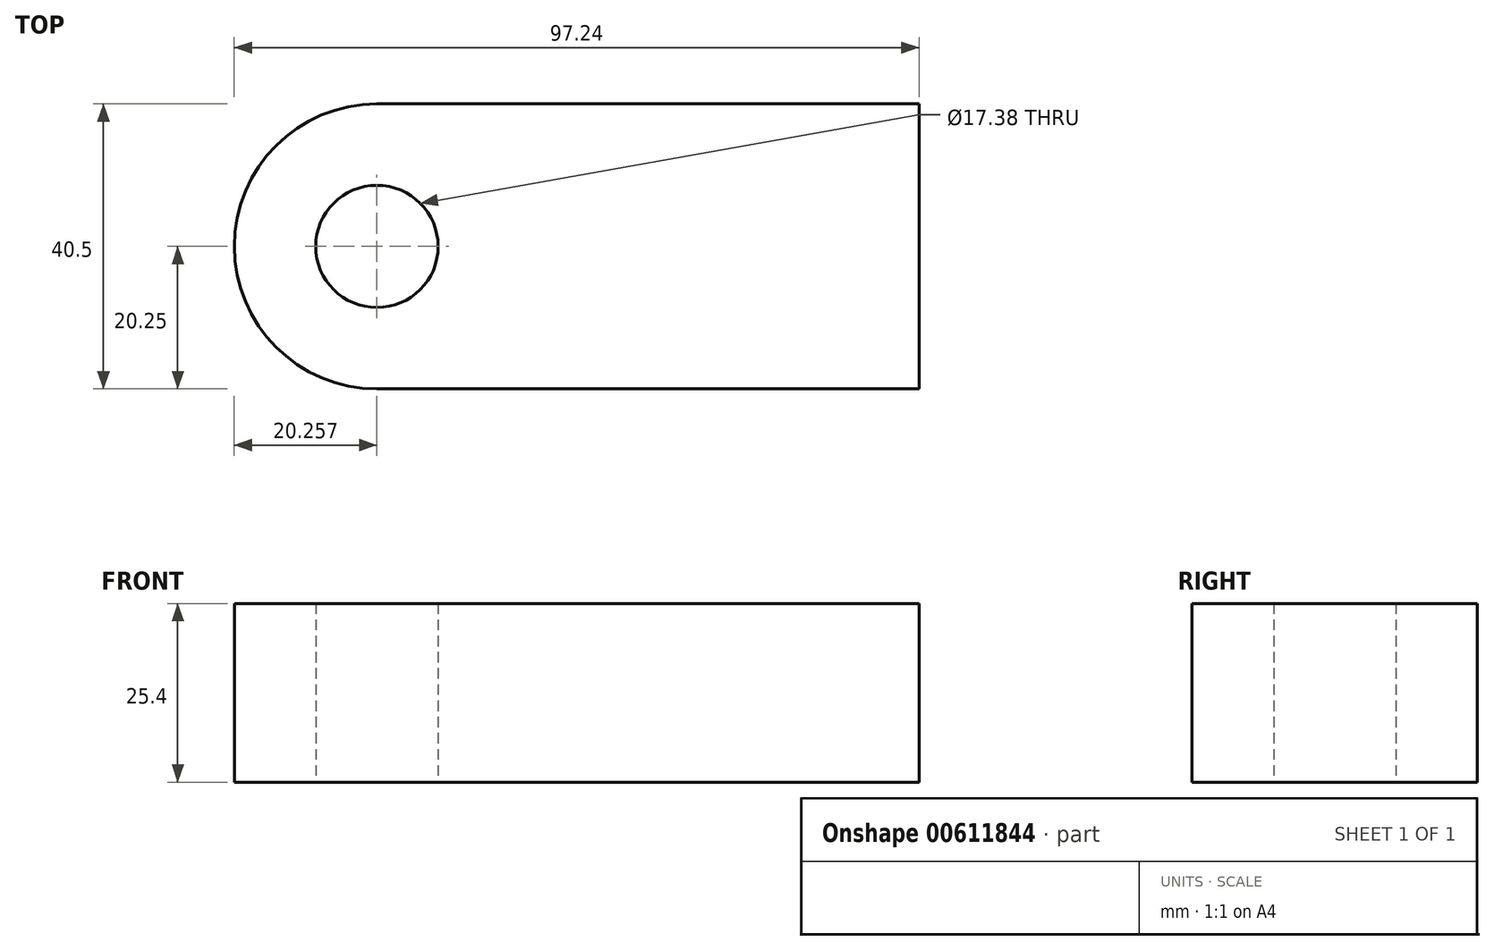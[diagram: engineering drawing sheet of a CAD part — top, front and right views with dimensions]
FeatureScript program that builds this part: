
annotation { "Feature Type Name" : "Feature", "Feature Type Description" : "" }
export const myFeature = defineFeature(function(context is Context, id is Id, definition is map)
    precondition{}
    {
        {
            var Q0;
            Q0=qCreatedBy(makeId("Top.planeOp"),FACE);
            var sketch = newSketch(context, id + "F0", { "sketchPlane" : qUnion([Q0])});
            skPoint(sketch, "E0.center.orphan", {"position": v(-43.75, 0) * mm});
            skLineSegment(sketch, "E1.bottom", {"start": v(-38.5, -20.25) * mm, "end": v(38.5, -20.25) * mm});
            skLineSegment(sketch, "E1.top", {"start": v(-38.5, 20.25) * mm, "end": v(38.5, 20.25) * mm});
            skLineSegment(sketch, "E1.right", {"start": v(38.5, -20.25) * mm, "end": v(38.5, 20.25) * mm});
            skPoint(sketch, "E1.middle", {"position": v(0, 0) * mm});
            skArc(sketch, "E2", {"start": v(-38.5, 20.25) * mm, "mid": v(-58.75, 0) * mm, "end": v(-38.5, -20.25) * mm});
            skCircle(sketch, "E3", {"center": v(-38.5, 0) * mm, "radius": 8.69 * mm});
            skSolve(sketch);
        }
        {
            var Q0;
            Q0 = qSketchRegion(id + "F0", true);
            extrude(context, id + "F1", {"entities" : qUnion([Q0]), "depth" : 25.4 * mm, "offsetDistance" : 25.4 * mm});
        }
    });
